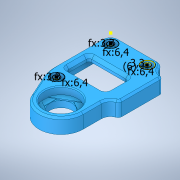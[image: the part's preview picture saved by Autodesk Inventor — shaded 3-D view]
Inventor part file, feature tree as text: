
AUTODESK INVENTOR PART (.ipt)
format: ipt  version: 2021.1 (Build 251245010, 245A)  size: 304,640 bytes
history: mixed  units: in
note: dims shown in document units (in); Inventor stores cm internally (conversion verified against a paired STEP export)
features: move_body x3, extrude x2, direct_edit x1, sketch x1, imported_body x1
ambient origin geometry x8: Origin, YZ Plane, XZ Plane, XY Plane, X Axis, Y Axis, Z Axis, Center Point
bodies: Solid1 (imported_parasolid), Body2 (imported_parasolid)
feature tree (8):
  direct_edit  "Direktbearbeitung1"
  sketch  "Skizze1"  dims[d0=0.0in d1=0.0in d2=-0.0138in d3=0.0in d4=0.0in d5=-0.0138in d6=0.0in d7=0.0in d8=-0.0138in d9=0.1299in d10=0.1299in d11=0.1299in d12=0.3937in d13=0.0in d14=0.2362in d15=0.252in d16=0.252in d17=0.252in d18=0.3937in d19=0.0in]
  extrude  "Extrusion1"  TaperAngle=0.0deg  [1 undecoded]
  extrude  "Extrusion2"  TaperAngle=0.0deg  [1 undecoded]
  move_body  "Verschieben1"
  move_body  "Verschieben2"
  move_body  "Verschieben3"
  imported_body  NMx_Import_Brep_tag  [imported B-rep: ~148 faces, bbox_mm=[34.6, 8.0, 53.550254]]
note: 2 required parameter values undecoded (feature->parameter linkage not recoverable at this tier; creation-order binding heuristic only, values carry confidence <= 0.55)
